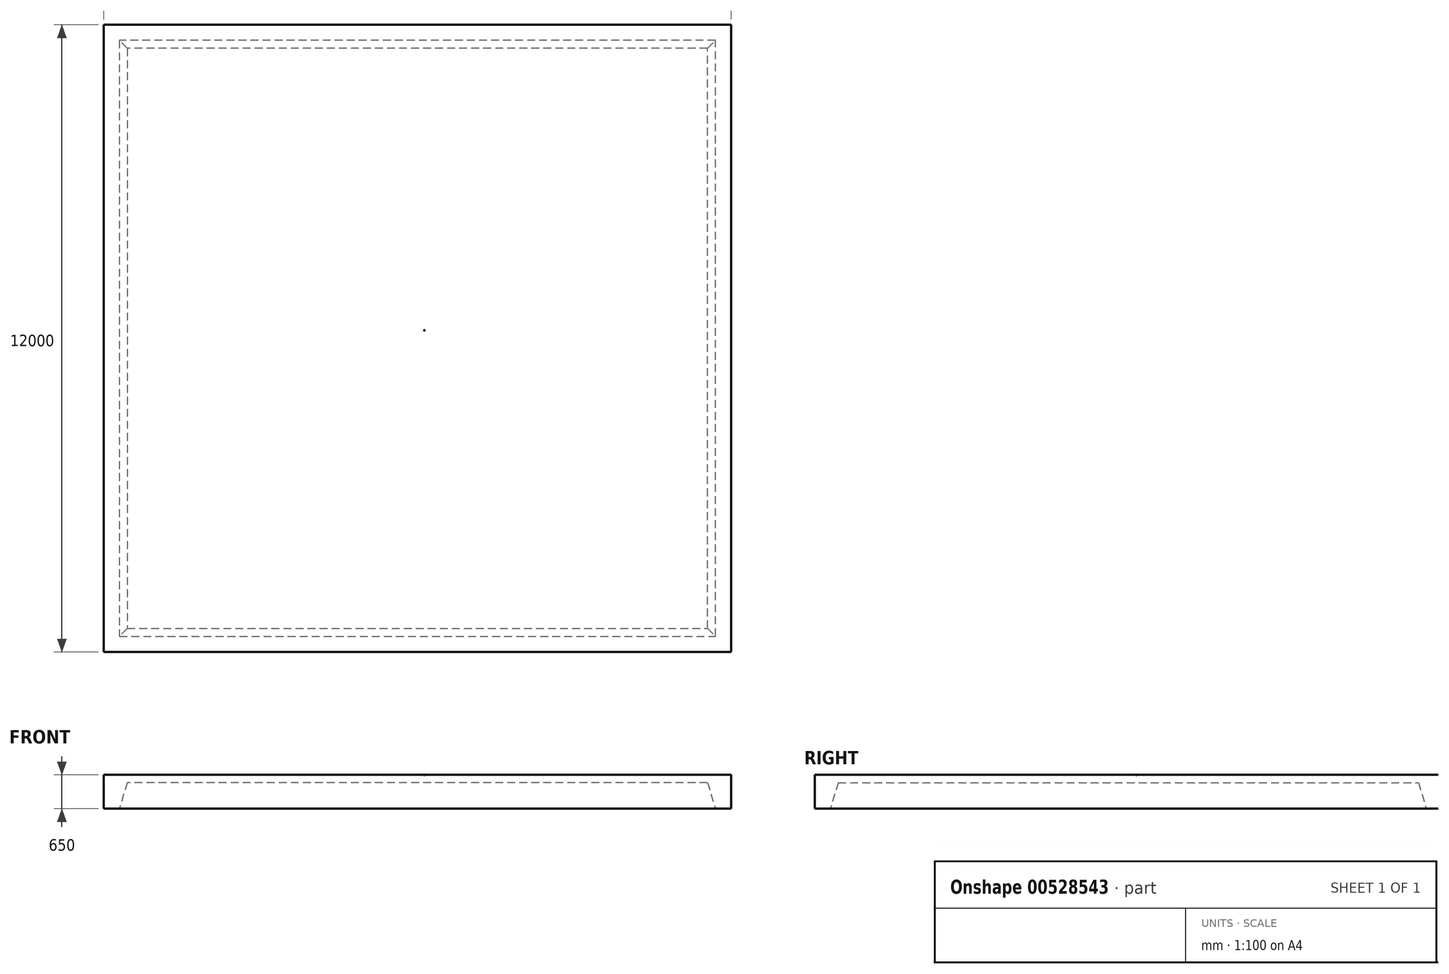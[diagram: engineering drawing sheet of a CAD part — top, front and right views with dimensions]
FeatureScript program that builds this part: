
annotation { "Feature Type Name" : "Feature", "Feature Type Description" : "" }
export const myFeature = defineFeature(function(context is Context, id is Id, definition is map)
    precondition{}
    {
        {
            var Q0;
            Q0=qCreatedBy(makeId("Top.planeOp"),FACE);
            var sketch = newSketch(context, id + "F0", { "sketchPlane" : qUnion([Q0])});
            skLineSegment(sketch, "E0.bottom", {"start": v(-6000, 6000) * mm, "end": v(6000, 6000) * mm});
            skLineSegment(sketch, "E0.top", {"start": v(-6000, -6000) * mm, "end": v(6000, -6000) * mm});
            skLineSegment(sketch, "E0.left", {"start": v(-6000, 6000) * mm, "end": v(-6000, -6000) * mm});
            skLineSegment(sketch, "E0.right", {"start": v(6000, 6000) * mm, "end": v(6000, -6000) * mm});
            skSolve(sketch);
        }
        {
            var Q0;
            Q0=qCreatedBy(makeId("Right.planeOp"),FACE);
            var sketch = newSketch(context, id + "F1", { "sketchPlane" : qUnion([Q0])});
            skLineSegment(sketch, "E1", {"start": v(-6000, 0) * mm, "end": v(-6000, -500) * mm});
            skLineSegment(sketch, "E2", {"start": v(-6000, -500) * mm, "end": v(-5700, -500) * mm});
            skLineSegment(sketch, "E3", {"start": v(-5700, -500) * mm, "end": v(-5550, 0) * mm});
            skLineSegment(sketch, "E4", {"start": v(-5550, 0) * mm, "end": v(-6000, 0) * mm});
            skSolve(sketch);
        }
        {
            var Q0;
            Q0=makeQuery(id+"F1.imprint","IMPRINT",FACE,{"disambiguationData":[TD([[makeQuery(id+"F1.imprint","IMPRINT",EDGE,{"derivedFrom":sQuery(id+"F1.wireOp",EDGE,"E1")}),1.0]])]});
            var Q1;
            Q1=sQuery(id+"F0.wireOp",EDGE,"E0.top");
            var Q2;
            Q2=sQuery(id+"F0.wireOp",EDGE,"E0.left");
            var Q3;
            Q3=sQuery(id+"F0.wireOp",EDGE,"E0.bottom");
            var Q4;
            Q4=sQuery(id+"F0.wireOp",EDGE,"E0.right");
            sweep(context, id + "F2", {"profiles" : qUnion([Q0]), "path" : qUnion([Q1, Q2, Q3, Q4])});
        }
        {
            var Q0;
            Q0=qSketchRegion(id+"F0",true);
            extrude(context, id + "F3", {"entities" : qUnion([Q0]), "operationType" : NewBodyOperationType.ADD, "depth" : 150 * mm, "offsetDistance" : 25 * mm});
        }
        {
            var Q0;
            Q0=makeQuery(id+"F3.opExtrude","CAP_FACE",FACE,{"disambiguationData":[OSD([sQuery(id+"F0.wireOp",EDGE,"E0.bottom"),sQuery(id+"F0.wireOp",EDGE,"E0.top"),sQuery(id+"F0.wireOp",EDGE,"E0.left"),sQuery(id+"F0.wireOp",EDGE,"E0.right")])],"isStart":false});
            var sketch = newSketch(context, id + "F4", { "sketchPlane" : qUnion([Q0])});
            skCircle(sketch, "E5", {"center": v(132.64, 152.2) * mm, "radius": 1201.04 * mm});
            skSolve(sketch);
        }
        {
            var Q0;
            Q0=sQuery(id+"F4.wireOp",VERTEX,"E5.center");
            var Q1;
            Q1=makeQuery(id+"F2.opSweep","SWEPT_BODY",BODY,{"disambiguationData":[OSD([sQuery(id+"F0.wireOp",EDGE,"E0.left"),sQuery(id+"F1.wireOp",EDGE,"E1"),sQuery(id+"F1.wireOp",EDGE,"E2"),sQuery(id+"F1.wireOp",EDGE,"E3"),sQuery(id+"F1.wireOp",EDGE,"E4")])]});
            hole(context, id + "F5", {"style" : HoleStyle.SIMPLE, "endStyle" : HoleEndStyle.BLIND, "standardTappedOrClearance" : lookupTablePath({ "standard" : "ANSI", "fit" : "Close", "size" : "1/2", "type" : "Clearance" }), "standardBlindInLast" : lookupTablePath({ "fit" : "Close", "standard" : "ANSI", "size" : "1/2", "type" : "Clearance" }), "holeDiameter" : 13.1 * mm, "holeDepth" : 20 * mm, "isTappedThrough" : true, "tappedDepth" : 12 * mm, "tapClearance" : 3, "startFromSketch" : true, "locations" : qUnion([Q0]), "scope" : qUnion([Q1])});
        }
    });
